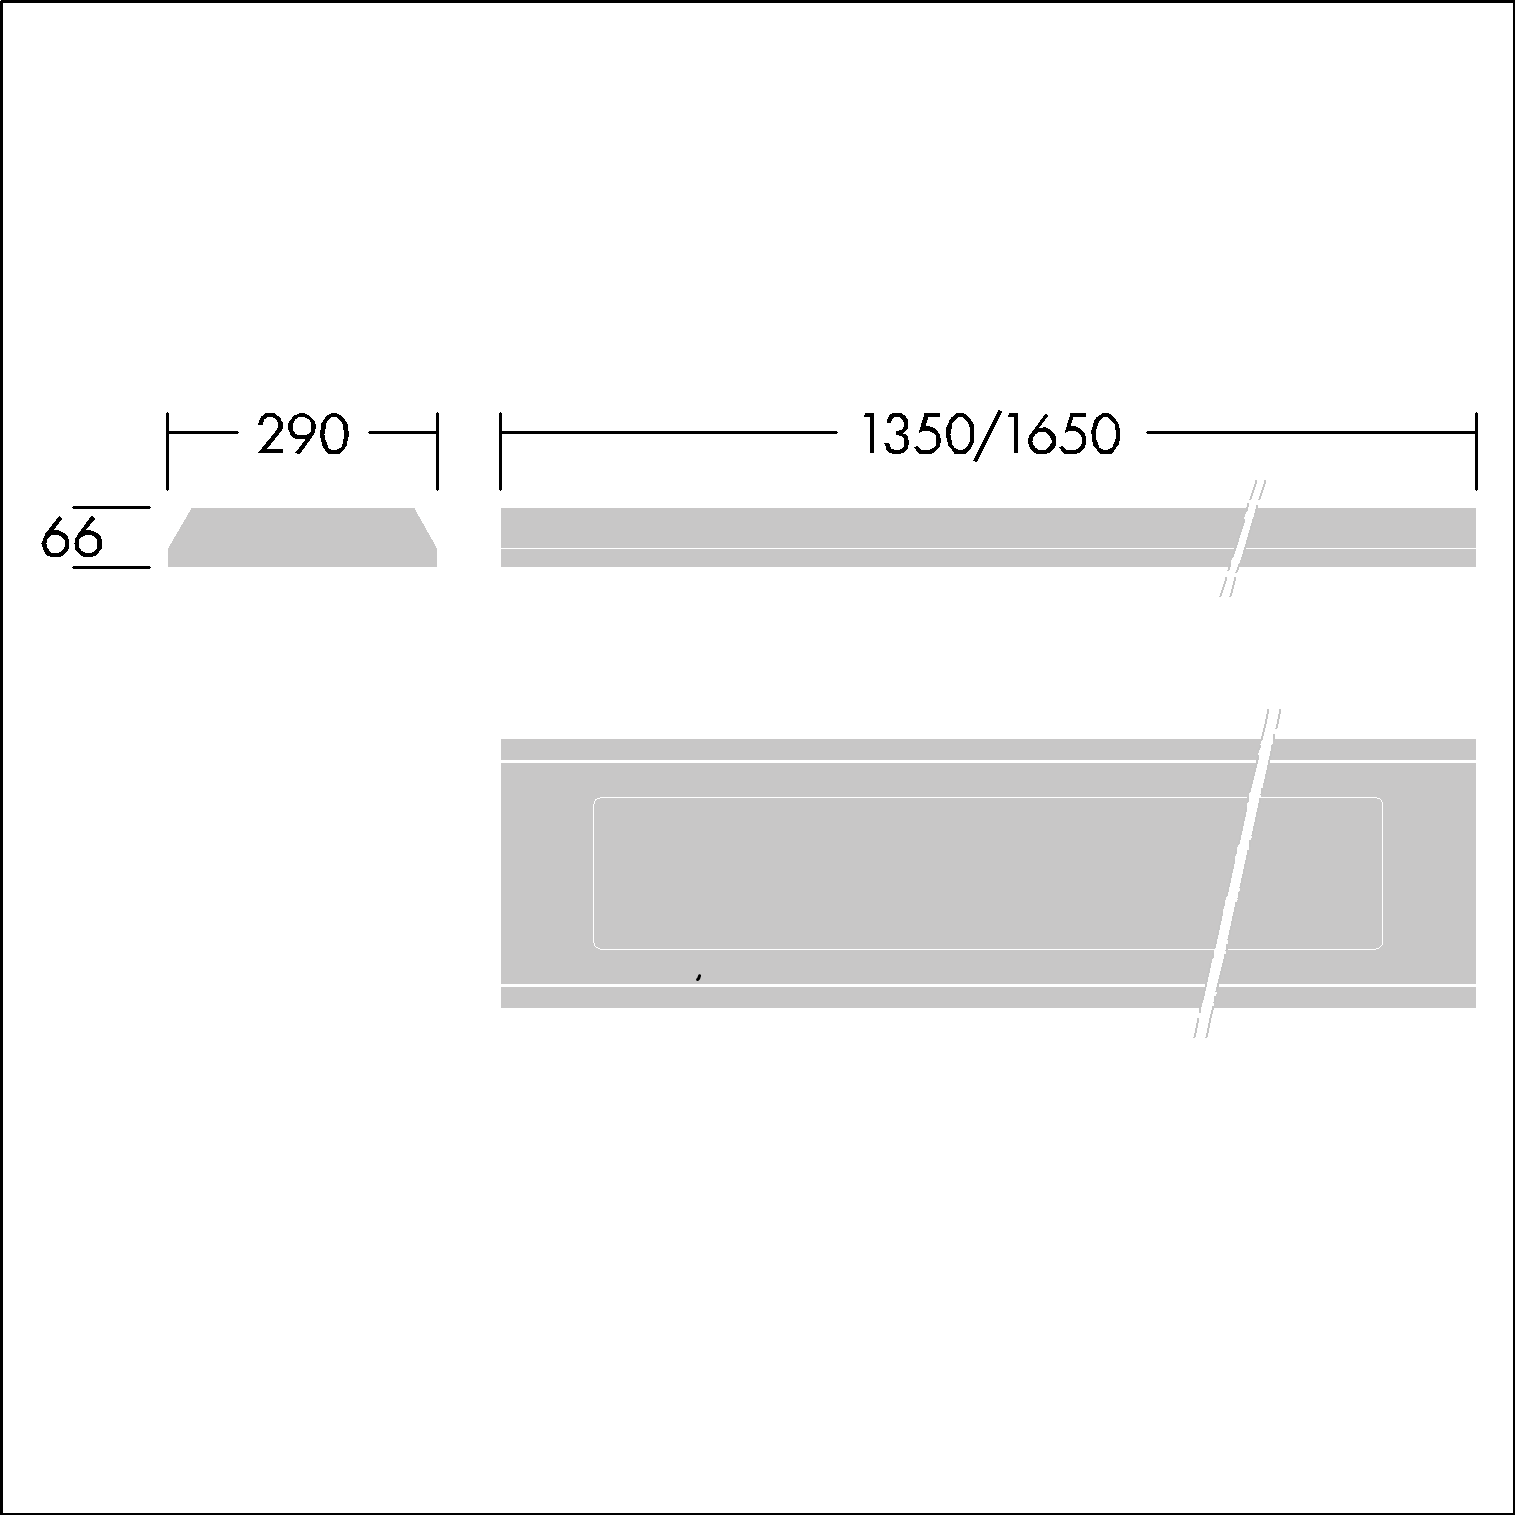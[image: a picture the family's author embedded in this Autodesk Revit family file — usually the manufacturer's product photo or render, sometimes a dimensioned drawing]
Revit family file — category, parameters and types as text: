
# Revit family: Thorn DUROLIGHT
name_source: partatom
category: Lighting Fixtures
revit_build: Autodesk Revit 2018 (Build: 20170223_1515(x64)
units: mm (PartAtom-declared; Revit-internal decimal feet)

## family parameters
Cut with Voids When Loaded = No
Host = Face
Light Source = Yes
OmniClass Number = 23.80.70.11
OmniClass Title = Luminaries for Internal Lighting
Part Type = Normal
Room Calculation Point = No
Round Connector Dimension = Use Diameter
Shared = No

## types (1)
- DUROLIGHT-S 5200-840 HF L1650
    Apparent Load = 48 VA
    Assembly Code = D5020200
    Body = Thorn_Metal_Light_Grey
    Color Filter = 16777215
    Cover = Thorn_PMMA
    Default Elevation = 0 mm  [stored 0 ft]
    Description = Surface mount LED luminaire
    Dimming Lamp Color Temperature Shift = <None>
    Emit Shape Visible in Rendering = No
    Emit from Rectangle Length = 164 mm  [stored 0.538058 ft]
    Emit from Rectangle Width = 1450 mm  [stored 4.75722 ft]
    Height = 66 mm
    Lamp = LED
    Length = 1650 mm  [stored 5.41339 ft]
    Manufacturer = Thorn Lighting
    Model = 96633062
    Photometric Web File = 96633062_(STD).IES
    Tilt Angle = -90.00°
    URL = www.thornlighting.com/96633062
    Voltage = 230 V
    Width = 290 mm  [stored 0.951444 ft]

note: [stored X ft] marks values corroborated as IEEE doubles in the binary element streams (Revit-internal decimal feet)

## geometry (parser evidence)
native form markers: Sweep x1
no freeform markers — native parametric forms only
